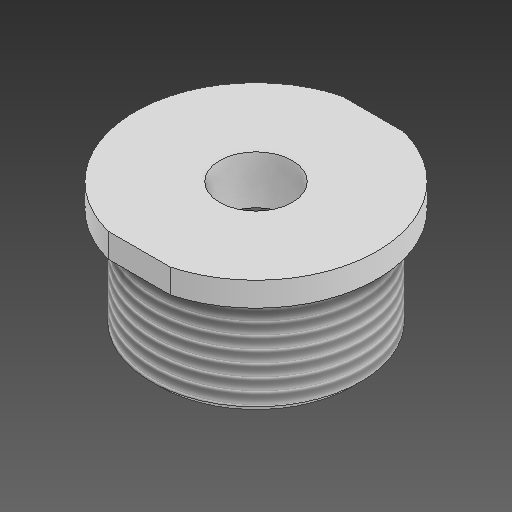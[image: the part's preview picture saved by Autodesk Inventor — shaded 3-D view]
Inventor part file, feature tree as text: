
AUTODESK INVENTOR PART (.ipt)
format: ipt  version: 2021 (Build 250183000, 183)  size: 175,616 bytes
history: native  units: mm
features: sketch x2, revolve x1, extrude x1, chamfer x1, thread x1
ambient origin geometry x8: Origin, YZ Plane, XZ Plane, XY Plane, X Axis, Y Axis, Z Axis, Center Point
bodies: Solid1 (feature_tree)
feature tree (6):
  revolve  "Revolution1"  [1 undecoded]
  extrude  "Extrusion1"  Depth=1.5mm
  chamfer  "Chamfer1"  Distance=15.0mm
  thread  "Thread3"  [1 undecoded]
  sketch  "Sketch1"  dims[d1=4.5mm d2=8.0mm]
  sketch  "Sketch2"  dims[d3=13.0mm d4=1.5mm d6=15.0mm d8=90.0deg d10=10.0mm d11=0.0mm d15=0.5mm d16=2.0mm d17=45.0deg d19=2.0mm d20=4.5mm d21=8.0mm d22=2.5mm d25=5.0mm d26=1.0mm d29=14.5mm d44=6.0mm d45=0.0mm]
note: 2 required parameter values undecoded (feature->parameter linkage not recoverable at this tier; creation-order binding heuristic only, values carry confidence <= 0.55)